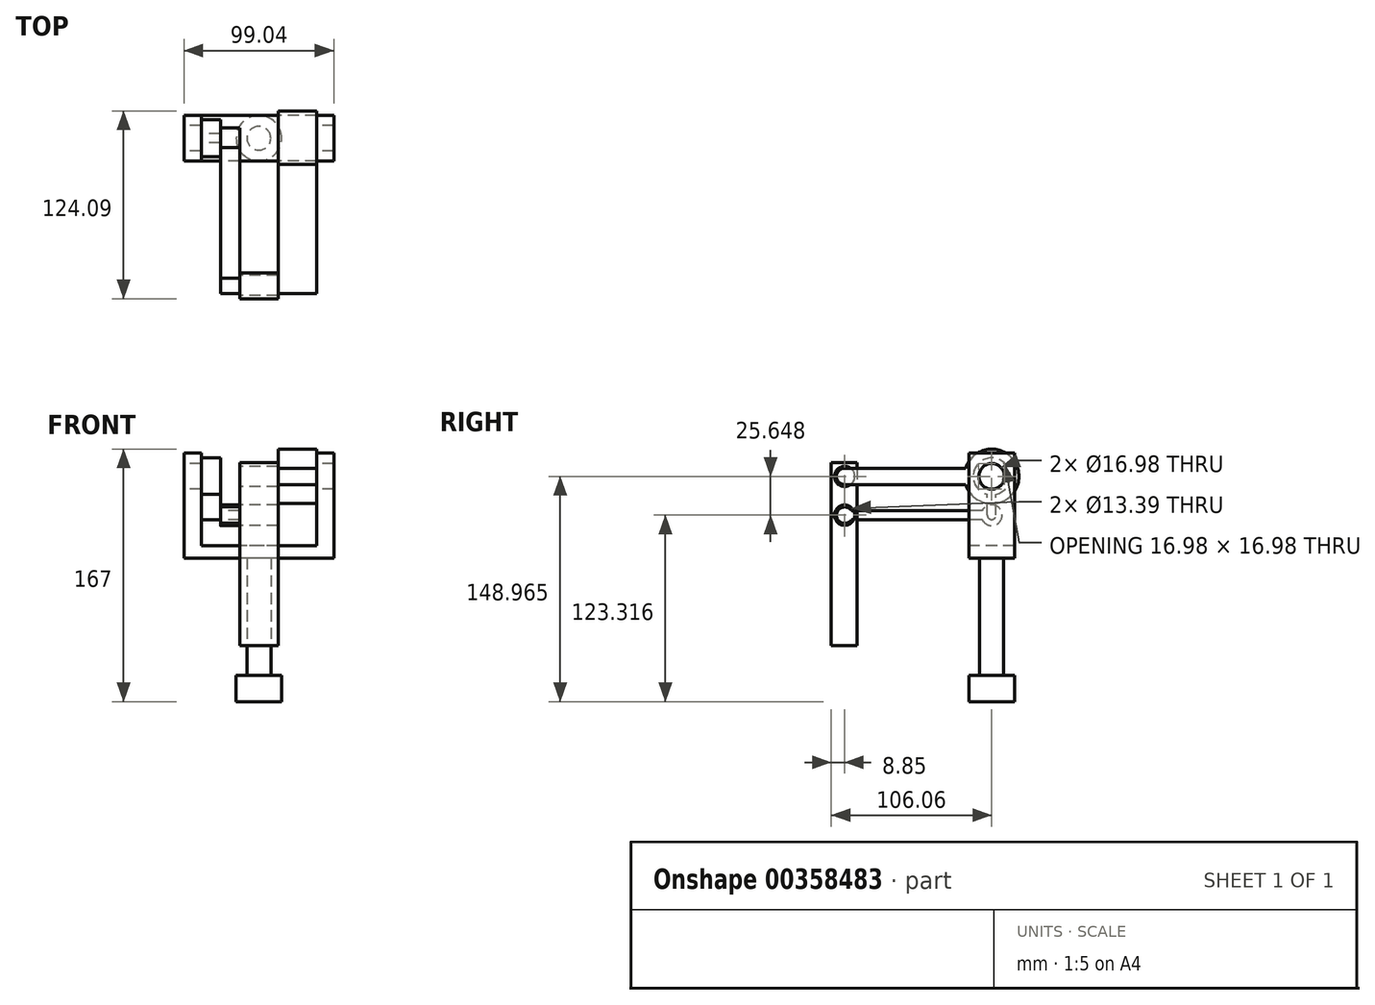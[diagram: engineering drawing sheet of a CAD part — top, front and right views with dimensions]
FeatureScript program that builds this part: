
annotation { "Feature Type Name" : "Feature", "Feature Type Description" : "" }
export const myFeature = defineFeature(function(context is Context, id is Id, definition is map)
    precondition{}
    {
        {
            var Q0;
            Q0=qCreatedBy(makeId("Top.planeOp"),FACE);
            var sketch = newSketch(context, id + "F0", { "sketchPlane" : qUnion([Q0])});
            skCircle(sketch, "E0", {"center": v(0, 0) * mm, "radius": 15.02 * mm});
            skSolve(sketch);
        }
        {
            var Q0;
            Q0 = qSketchRegion(id + "F0", true);
            extrude(context, id + "F1", {"entities" : qUnion([Q0]), "depth" : 17.53 * mm});
        }
        {
            var Q0;
            Q0=makeQuery(id+"F1.opExtrude","CAP_FACE",FACE,{"disambiguationData":[OSD([sQuery(id+"F0.wireOp",EDGE,"E0")])],"isStart":false});
            var sketch = newSketch(context, id + "F2", { "sketchPlane" : qUnion([Q0])});
            skCircle(sketch, "E1", {"center": v(0, 0) * mm, "radius": 7.91 * mm});
            skSolve(sketch);
        }
        {
            var Q0;
            Q0 = qSketchRegion(id + "F2", true);
            extrude(context, id + "F3", {"entities" : qUnion([Q0]), "depth" : 77.47 * mm});
        }
        {
            var Q0;
            Q0=makeQuery(id+"F3.opExtrude","CAP_FACE",FACE,{"disambiguationData":[OSD([sQuery(id+"F2.wireOp",EDGE,"E1")])],"isStart":false});
            var sketch = newSketch(context, id + "F4", { "sketchPlane" : qUnion([Q0])});
            skLineSegment(sketch, "E2.bottom", {"start": v(49.52, -15.1) * mm, "end": v(-49.52, -15.1) * mm});
            skLineSegment(sketch, "E2.top", {"start": v(49.52, 15.1) * mm, "end": v(-49.52, 15.1) * mm});
            skLineSegment(sketch, "E2.left", {"start": v(49.52, -15.1) * mm, "end": v(49.52, 15.1) * mm});
            skLineSegment(sketch, "E2.right", {"start": v(-49.52, -15.1) * mm, "end": v(-49.52, 15.1) * mm});
            skPoint(sketch, "E2.middle", {"position": v(0, 0) * mm});
            skSolve(sketch);
        }
        {
            var Q0;
            Q0 = qSketchRegion(id + "F4", true);
            extrude(context, id + "F5", {"entities" : qUnion([Q0]), "operationType" : NewBodyOperationType.ADD, "depth" : 8.13 * mm});
        }
        {
            var Q0;
            Q0=makeQuery(id+"F5.opExtrude","CAP_FACE",FACE,{"disambiguationData":[OSD([sQuery(id+"F4.wireOp",EDGE,"E2.bottom"),sQuery(id+"F4.wireOp",EDGE,"E2.top"),sQuery(id+"F4.wireOp",EDGE,"E2.left"),sQuery(id+"F4.wireOp",EDGE,"E2.right")])],"isStart":false});
            var sketch = newSketch(context, id + "F6", { "sketchPlane" : qUnion([Q0])});
            skLineSegment(sketch, "E3.bottom", {"start": v(-49.52, 15.1) * mm, "end": v(-38.1, 15.1) * mm});
            skLineSegment(sketch, "E3.top", {"start": v(-49.52, -15.1) * mm, "end": v(-38.1, -15.1) * mm});
            skLineSegment(sketch, "E3.left", {"start": v(-49.52, 15.1) * mm, "end": v(-49.52, -15.1) * mm});
            skLineSegment(sketch, "E3.right", {"start": v(-38.1, 15.1) * mm, "end": v(-38.1, -15.1) * mm});
            skLineSegment(sketch, "E4.bottom", {"start": v(49.52, 15.1) * mm, "end": v(38.1, 15.1) * mm});
            skLineSegment(sketch, "E4.top", {"start": v(49.52, -15.1) * mm, "end": v(38.1, -15.1) * mm});
            skLineSegment(sketch, "E4.left", {"start": v(49.52, 15.1) * mm, "end": v(49.52, -15.1) * mm});
            skLineSegment(sketch, "E4.right", {"start": v(38.1, 15.1) * mm, "end": v(38.1, -15.1) * mm});
            skSolve(sketch);
        }
        {
            var Q0;
            Q0 = qSketchRegion(id + "F6", true);
            extrude(context, id + "F7", {"entities" : qUnion([Q0]), "operationType" : NewBodyOperationType.ADD, "depth" : 61.2 * mm});
        }
        {
            var Q0;
            Q0=makeQuery(id+"F7.boolean.opBoolean","MERGE",FACE,{"derivedFrom":[makeQuery(id+"F5.opExtrude","SWEPT_FACE",FACE,{"disambiguationData":[OSD([sQuery(id+"F4.wireOp",EDGE,"E2.right")])]}),makeQuery(id+"F7.opExtrude","SWEPT_FACE",FACE,{"disambiguationData":[OSD([sQuery(id+"F6.wireOp",EDGE,"E3.left")])]})]});
            var sketch = newSketch(context, id + "F8", { "sketchPlane" : qUnion([Q0])});
            skCircle(sketch, "E5", {"center": v(0, 148.96) * mm, "radius": 8.49 * mm});
            skSolve(sketch);
        }
        {
            var Q0;
            Q0 = qSketchRegion(id + "F8", true);
            extrude(context, id + "F9", {"entities" : qUnion([Q0]), "operationType" : NewBodyOperationType.REMOVE, "endBound" : BoundingType.THROUGH_ALL, "oppositeDirection" : true, "depth" : 25.4 * mm});
        }
        {
            var Q0;
            Q0=makeQuery(id+"F7.opExtrude","SWEPT_FACE",FACE,{"disambiguationData":[OSD([sQuery(id+"F6.wireOp",EDGE,"E3.right")])]});
            var sketch = newSketch(context, id + "F10", { "sketchPlane" : qUnion([Q0])});
            skCircle(sketch, "E6", {"center": v(0, 148.96) * mm, "radius": 12.24 * mm});
            skLineSegment(sketch, "E7.bottom", {"start": v(2.9, 123.32) * mm, "end": v(-2.9, 123.32) * mm});
            skLineSegment(sketch, "E7.top", {"start": v(2.9, 157.63) * mm, "end": v(-2.9, 157.63) * mm});
            skLineSegment(sketch, "E7.left", {"start": v(2.9, 123.32) * mm, "end": v(2.9, 157.63) * mm});
            skLineSegment(sketch, "E7.right", {"start": v(-2.9, 123.32) * mm, "end": v(-2.9, 157.63) * mm});
            skPoint(sketch, "E7.middle", {"position": v(0, 140.48) * mm});
            skCircle(sketch, "E8", {"center": v(0, 123.32) * mm, "radius": 2.9 * mm});
            skSolve(sketch);
        }
        {
            var Q0;
            Q0 = qSketchRegion(id + "F10", true);
            extrude(context, id + "F11", {"entities" : qUnion([Q0]), "depth" : 12.7 * mm});
        }
        {
            var Q0;
            Q0=makeQuery(id+"F7.opExtrude","SWEPT_FACE",FACE,{"disambiguationData":[OSD([sQuery(id+"F6.wireOp",EDGE,"E4.right")])]});
            var sketch = newSketch(context, id + "F12", { "sketchPlane" : qUnion([Q0])});
            skCircle(sketch, "E9", {"center": v(0, 148.96) * mm, "radius": 18.03 * mm});
            skLineSegment(sketch, "E10.bottom", {"start": v(-4.04, 143.56) * mm, "end": v(97.2, 143.56) * mm});
            skLineSegment(sketch, "E10.top", {"start": v(-4.04, 154.37) * mm, "end": v(97.2, 154.37) * mm});
            skLineSegment(sketch, "E10.left", {"start": v(-4.04, 143.56) * mm, "end": v(-4.04, 154.37) * mm});
            skLineSegment(sketch, "E10.right", {"start": v(97.2, 143.56) * mm, "end": v(97.2, 154.37) * mm});
            skPoint(sketch, "E10.middle", {"position": v(46.58, 148.96) * mm});
            skCircle(sketch, "E11", {"center": v(97.2, 148.96) * mm, "radius": 5.4 * mm});
            skSolve(sketch);
        }
        {
            var Q0;
            Q0 = qSketchRegion(id + "F12", true);
            extrude(context, id + "F13", {"entities" : qUnion([Q0]), "depth" : 25.4 * mm});
        }
        {
            var Q0;
            Q0=makeQuery(id+"F11.opExtrude","CAP_FACE",FACE,{"disambiguationData":[OSD([sQuery(id+"F10.wireOp",EDGE,"E6"),sQuery(id+"F10.wireOp",EDGE,"E7.left"),sQuery(id+"F10.wireOp",EDGE,"E7.right"),sQuery(id+"F10.wireOp",EDGE,"E8")])],"isStart":false});
            var sketch = newSketch(context, id + "F14", { "sketchPlane" : qUnion([Q0])});
            skCircle(sketch, "E12", {"center": v(0, 123.32) * mm, "radius": 6.93 * mm});
            skCircle(sketch, "E13", {"center": v(-97.2, 123.32) * mm, "radius": 5.4 * mm});
            skLineSegment(sketch, "E14", {"start": v(-102.62, 158.34) * mm, "end": v(-102.62, 105.75) * mm, "construction": true});
            skLineSegment(sketch, "E15.bottom", {"start": v(0, 120.34) * mm, "end": v(-97.2, 120.34) * mm});
            skLineSegment(sketch, "E15.top", {"start": v(0, 126.3) * mm, "end": v(-97.2, 126.3) * mm});
            skLineSegment(sketch, "E15.left", {"start": v(0, 120.34) * mm, "end": v(0, 126.3) * mm});
            skLineSegment(sketch, "E15.right", {"start": v(-97.2, 120.34) * mm, "end": v(-97.2, 126.3) * mm});
            skPoint(sketch, "E15.middle", {"position": v(-48.6, 123.32) * mm});
            skSolve(sketch);
        }
        {
            var Q0;
            Q0 = qSketchRegion(id + "F14", true);
            var Q1;
            Q1=qCreatedBy(makeId("Right.planeOp"),FACE);
            extrude(context, id + "F15", {"entities" : qUnion([Q0]), "endBoundEntityFace" : qUnion([Q1]), "depth" : 12.7 * mm});
        }
        {
            var Q0;
            Q0=qCreatedBy(makeId("Right.planeOp"),FACE);
            var sketch = newSketch(context, id + "F16", { "sketchPlane" : qUnion([Q0])});
            skLineSegment(sketch, "E16.bottom", {"start": v(-106.06, 158.2) * mm, "end": v(-88.94, 158.2) * mm});
            skLineSegment(sketch, "E16.top", {"start": v(-106.06, 37.1) * mm, "end": v(-88.94, 37.1) * mm});
            skLineSegment(sketch, "E16.left", {"start": v(-106.06, 158.2) * mm, "end": v(-106.06, 37.1) * mm});
            skLineSegment(sketch, "E16.right", {"start": v(-88.94, 158.2) * mm, "end": v(-88.94, 37.1) * mm});
            skCircle(sketch, "E17", {"center": v(-97.2, 148.96) * mm, "radius": 6.7 * mm});
            skCircle(sketch, "E18", {"center": v(-97.2, 123.32) * mm, "radius": 6.7 * mm});
            skSolve(sketch);
        }
        {
            var Q0;
            Q0 = qSketchRegion(id + "F16", true);
            extrude(context, id + "F17", {"entities" : qUnion([Q0]), "depth" : 25.4 * mm, "symmetric" : true});
        }
    });
